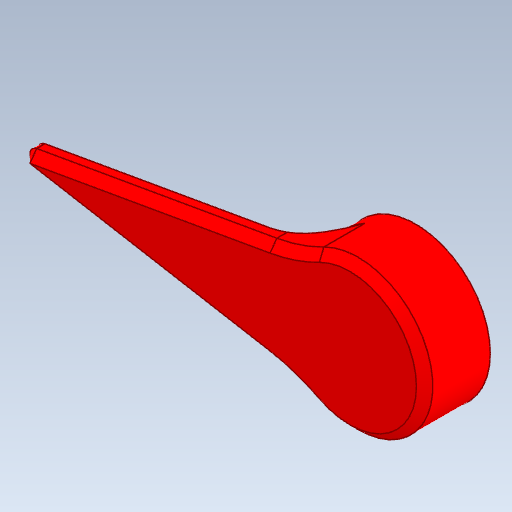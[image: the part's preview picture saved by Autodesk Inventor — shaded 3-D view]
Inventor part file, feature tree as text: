
AUTODESK INVENTOR PART (.ipt)
format: ipt  version: 2021.2 (Build 252289000, 289)  size: 159,232 bytes
history: native  units: mm
features: extrude x3, other x1, sketch x1, fillet x1, chamfer x1
ambient origin geometry x8: Origin, YZ Plane, XZ Plane, XY Plane, X Axis, Y Axis, Z Axis, Center Point
bodies: Body1 (feature_tree)
feature tree (7):
  other  "Твердое тело1"
  sketch  "Эскиз1"
  extrude  "Выдавливание1"  Depth=6.7mm
  extrude  "Выдавливание3"  Depth=1.2mm
  extrude  "Выдавливание4"  Depth=40.0mm
  fillet  "Сопряжение1"  Radius=0.5mm
  chamfer  "Фаска1"  Distance=3.490659mm
